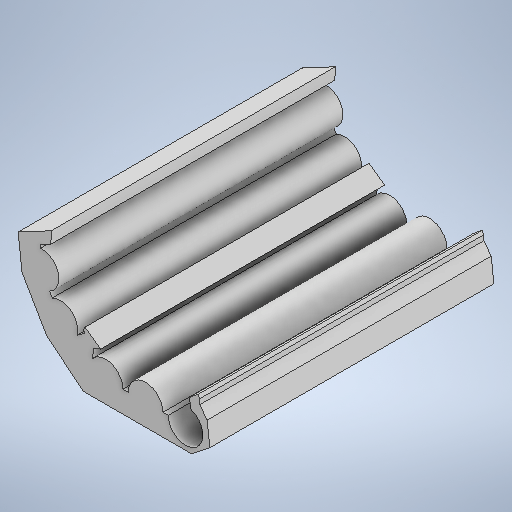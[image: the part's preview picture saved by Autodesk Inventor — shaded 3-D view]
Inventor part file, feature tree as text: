
AUTODESK INVENTOR PART (.ipt)
format: ipt  version: 2025.2 (Build 292293000, 293)  size: 293,888 bytes
history: native  units: mm
features: extrude x1, sketch x1
ambient origin geometry x8: Origin, YZ Plane, XZ Plane, XY Plane, X Axis, Y Axis, Z Axis, Center Point
bodies: Solid1 (feature_tree)
feature tree (2):
  extrude  "Extrusion1"  Depth=213.0mm
  sketch  "Sketch1"  dims[d0=26.0mm d1=40.0mm d2=26.0mm d3=30.0mm d4=26.0mm d5=30.0mm d6=26.0mm d7=30.0mm d8=26.0mm d11=25.830873mm d12=150.0deg d15=213.0mm d16=0.0mm]
